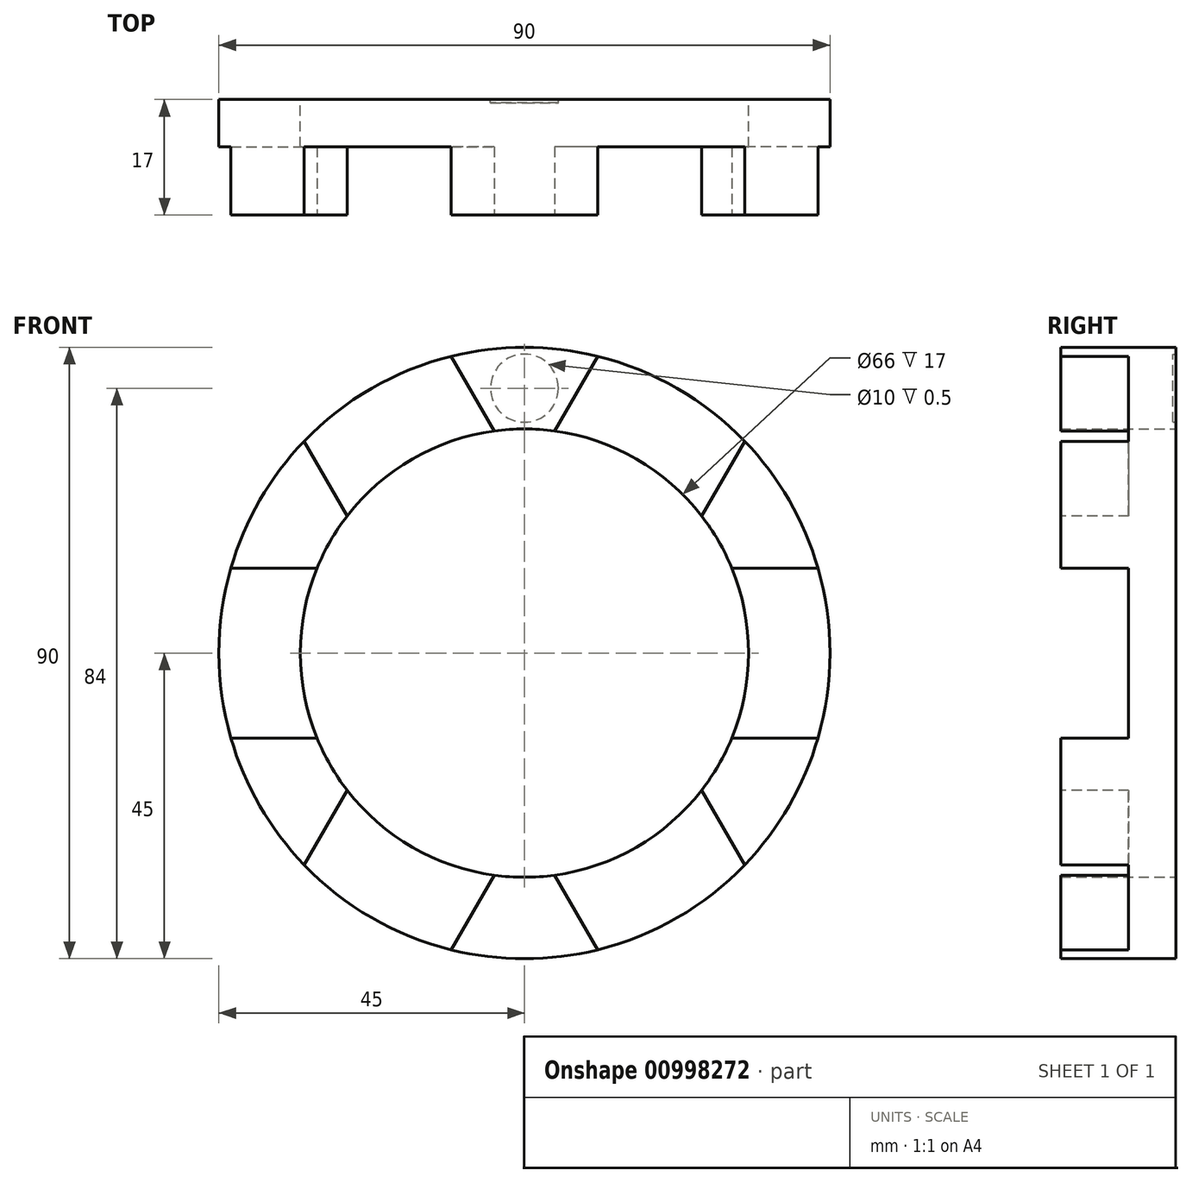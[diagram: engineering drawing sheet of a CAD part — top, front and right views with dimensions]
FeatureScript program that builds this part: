
annotation { "Feature Type Name" : "Feature", "Feature Type Description" : "" }
export const myFeature = defineFeature(function(context is Context, id is Id, definition is map)
    precondition{}
    {
        {
            var Q0;
            Q0=qCreatedBy(makeId("Front.planeOp"),FACE);
            var sketch = newSketch(context, id + "F0", { "sketchPlane" : qUnion([Q0])});
            skCircle(sketch, "E0", {"center": v(0, 0) * mm, "radius": 45 * mm});
            skLineSegment(sketch, "E1", {"start": v(0, 0) * mm, "end": v(0, 33) * mm, "construction": true});
            skCircle(sketch, "E2", {"center": v(0, 0) * mm, "radius": 33 * mm});
            skSolve(sketch);
        }
        {
            var Q0;
            Q0=makeQuery(id+"F0.imprint","IMPRINT",FACE,{"disambiguationData":[TD([[makeQuery(id+"F0.imprint","IMPRINT",EDGE,{"derivedFrom":sQuery(id+"F0.wireOp",EDGE,"E0")}),1.0]])]});
            extrude(context, id + "F1", {"entities" : qUnion([Q0]), "depth" : 17 * mm, "offsetDistance" : 25 * mm});
        }
        {
            var Q0;
            Q0=qCreatedBy(makeId("Front.planeOp"),FACE);
            var sketch = newSketch(context, id + "F2", { "sketchPlane" : qUnion([Q0])});
            skLineSegment(sketch, "E3", {"start": v(0, 0) * mm, "end": v(0, 39) * mm, "construction": true});
            skCircle(sketch, "E4", {"center": v(0, 39) * mm, "radius": 5 * mm});
            skSolve(sketch);
        }
        {
            var Q0;
            Q0=makeQuery(id+"F2.imprint","IMPRINT",FACE,{"disambiguationData":[TD([[makeQuery(id+"F2.imprint","IMPRINT",EDGE,{"derivedFrom":sQuery(id+"F2.wireOp",EDGE,"E4")}),1.0]])]});
            extrude(context, id + "F3", {"entities" : qUnion([Q0]), "operationType" : NewBodyOperationType.REMOVE, "depth" : 0.5 * mm, "offsetDistance" : 25 * mm});
        }
        {
            var Q0;
            Q0=qCreatedBy(makeId("Top.planeOp"),FACE);
            var sketch = newSketch(context, id + "F4", { "sketchPlane" : qUnion([Q0])});
            skLineSegment(sketch, "E5", {"start": v(0, 0) * mm, "end": v(0, -30.02) * mm, "construction": true});
            skSolve(sketch);
        }
        {
            var Q0;
            Q0=makeQuery(id+"F1.opExtrude","CAP_FACE",FACE,{"disambiguationData":[OSD([sQuery(id+"F0.wireOp",EDGE,"E0"),sQuery(id+"F0.wireOp",EDGE,"E2")])],"isStart":false});
            var sketch = newSketch(context, id + "F5", { "sketchPlane" : qUnion([Q0])});
            skLineSegment(sketch, "E6.bottom", {"start": v(-50.5, 12.5) * mm, "end": v(-15.5, 12.5) * mm});
            skLineSegment(sketch, "E6.top", {"start": v(-50.5, -12.5) * mm, "end": v(-15.5, -12.5) * mm});
            skLineSegment(sketch, "E6.left", {"start": v(-50.5, 12.5) * mm, "end": v(-50.5, -12.5) * mm});
            skLineSegment(sketch, "E6.right", {"start": v(-15.5, 12.5) * mm, "end": v(-15.5, -12.5) * mm});
            skPoint(sketch, "E6.middle", {"position": v(-33, 0) * mm});
            skSolve(sketch);
        }
        {
            var Q0;
            {var subQ0=sQuery(id+"F5.wireOp",EDGE,"E6.bottom");var subQ1=makeQuery(id+"F1.opExtrude","CAP_EDGE",EDGE,{"disambiguationData":[OSD([sQuery(id+"F0.wireOp",EDGE,"E0")])],"isStart":false});var subQ2=makeQuery(id+"F5.imprint","INTERSECT",VERTEX,{"derivedFrom":[subQ1,subQ0]});Q0=makeQuery(id+"F5.imprint","IMPRINT",FACE,{"disambiguationData":[TD([[makeQuery(id+"F5.imprint","IMPRINT",EDGE,{"disambiguationData":[TD([[subQ2,-1.0]])],"derivedFrom":subQ0}),-1.0]])]});}
            extrude(context, id + "F6", {"entities" : qUnion([Q0]), "operationType" : NewBodyOperationType.REMOVE, "oppositeDirection" : true, "depth" : 10 * mm, "offsetDistance" : 25 * mm});
        }
        {
            var Q0;
            Q0=qCreatedBy(makeId("Top.planeOp"),FACE);
            var sketch = newSketch(context, id + "F7", { "sketchPlane" : qUnion([Q0])});
            skLineSegment(sketch, "E7", {"start": v(0, 0) * mm, "end": v(0, -40.23) * mm, "construction": true});
            skSolve(sketch);
        }
        {
            var Q0;
            Q0=makeQuery(id+"F6.boolean.opBoolean","COPY",FACE,{"derivedFrom":makeQuery(id+"F6.opExtrude","SWEPT_FACE",FACE,{"disambiguationData":[OSD([sQuery(id+"F5.wireOp",EDGE,"E6.bottom")])]})});
            var Q1;
            Q1=makeQuery(id+"F6.boolean.opBoolean","COPY",FACE,{"derivedFrom":makeQuery(id+"F6.opExtrude","CAP_FACE",FACE,{"disambiguationData":[OSD([sQuery(id+"F0.wireOp",EDGE,"E0"),sQuery(id+"F0.wireOp",EDGE,"E2"),sQuery(id+"F5.wireOp",EDGE,"E6.bottom"),sQuery(id+"F5.wireOp",EDGE,"E6.top")])],"isStart":false})});
            var Q2;
            Q2=makeQuery(id+"F6.boolean.opBoolean","COPY",FACE,{"derivedFrom":makeQuery(id+"F6.opExtrude","SWEPT_FACE",FACE,{"disambiguationData":[OSD([sQuery(id+"F5.wireOp",EDGE,"E6.top")])]})});
            var Q3;
            Q3=sQuery(id+"F7.wireOp",EDGE,"E7");
            circularPattern(context, id + "F8", {"patternType" : PatternType.FACE, "faces" : qUnion([Q0, Q1, Q2]), "axis" : qUnion([Q3]), "angle" : 360 * degree, "instanceCount" : 6, "equalSpace" : true});
        }
    });
